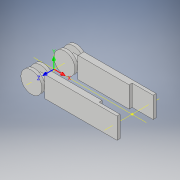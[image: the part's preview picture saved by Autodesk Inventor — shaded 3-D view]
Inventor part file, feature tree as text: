
AUTODESK INVENTOR PART (.ipt)
format: ipt  version: 2019 (Build 230136000, 136)  size: 163,840 bytes
history: native  units: in
note: dims shown in document units (in); Inventor stores cm internally (conversion verified against a paired STEP export)
features: other x8, extrude x4, sketch x4, plane x2, mirror x1
ambient origin geometry x4: Origin, YZ Plane, XZ Plane, XY Plane
bodies: Solid1 (feature_tree)
feature tree (19):
  plane  "Work Plane1"
  extrude  "Extrusion1"  Depth=2.2047in
  extrude  "Extrusion2"  Depth=0.9449in
  extrude  "Extrusion3"  Depth=7.5591in
  extrude  "Extrusion4"  Depth=0.6299in TaperAngle=0.0deg
  mirror  "Mirror2"
  other  "Work Point2"
  sketch  "Sketch2"  dims[d1=1.1024in d2=2.2047in]
  sketch  "Sketch3"  dims[d3=0.315in d4=0.0in d5=0.9449in]
  sketch  "Sketch4"  dims[d6=1.1024in d7=7.5591in]
  sketch  "Sketch5"  dims[d8=2.2047in d9=0.6299in d10=0.0in d11=0.315in d12=0.0in d13=2.2047in d14=0.315in d15=0.0in d16=0.4724in d17=1.1024in d18=0.0in d19=0.0in d20=0.0in d21=0.0in d22=0.0in d23=0.0in]
  plane  "Work Plane3"
  other  "UCS2: YZ Plane"
  other  "UCS2: XZ Plane"
  other  "UCS2: XY Plane"
  other  "UCS2: X Axis"
  other  "UCS2: Y Axis"
  other  "UCS2: Z Axis"
  other  "UCS2: Center Point"
